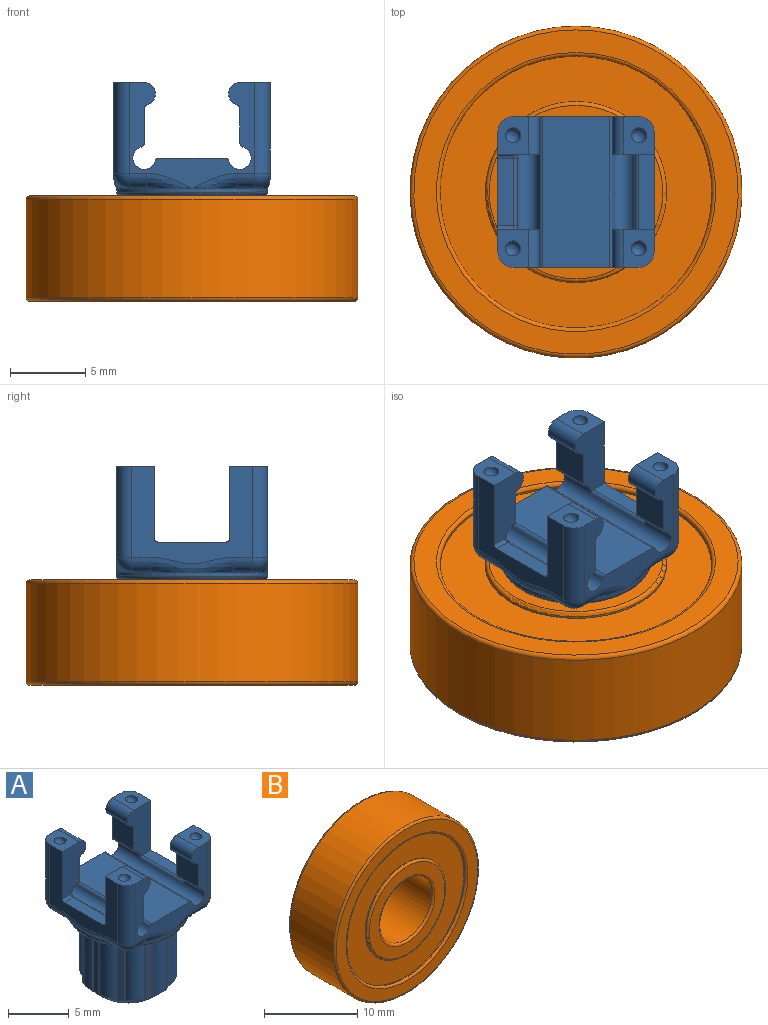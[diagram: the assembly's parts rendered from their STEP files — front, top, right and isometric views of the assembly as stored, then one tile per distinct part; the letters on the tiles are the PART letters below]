
ASSEMBLY  parts=2 mates=1
PART A: 118 faces, bbox 11x11x14.6 mm
  f0: plane 1.25x1.18mm, normal (0,0,-1), area 0.6mm2, adj f39,f105,f110
  f1: plane 1.25x1.18mm, normal (0,0,-1), area 0.6mm2, adj f39,f98,f101
  f2: cylinder r=3.75mm len=6.25mm, axis (0,0,1), area 3.5mm2, adj f40,f52,f88,f90
  f3: cylinder r=3.75mm len=6.25mm, axis (0,0,1), area 3.5mm2, adj f40,f85,f89,f90
  f4: cylinder r=3.75mm len=6.25mm, axis (0,0,1), area 3.5mm2, adj f40,f82,f86,f90
  f5: cylinder r=3.75mm len=6.25mm, axis (0,0,1), area 3.5mm2, adj f40,f79,f83,f90
  f6: cylinder r=3.75mm len=6.25mm, axis (0,0,1), area 3.5mm2, adj f40,f76,f80,f90
  f7: cylinder r=3.75mm len=6.25mm, axis (0,0,1), area 3.5mm2, adj f40,f73,f77,f90
  f8: cylinder r=3.75mm len=6.25mm, axis (0,0,1), area 3.5mm2, adj f40,f70,f74,f90
  f9: cylinder r=3.75mm len=6.25mm, axis (0,0,1), area 3.5mm2, adj f40,f67,f71,f90
  f10: cylinder r=3.75mm len=6.25mm, axis (0,0,1), area 3.5mm2, adj f40,f64,f68,f90
  f11: cylinder r=3.75mm len=6.25mm, axis (0,0,1), area 3.5mm2, adj f40,f51,f65,f90
  f12: plane 1.25x1.18mm, normal (0,0,-1), area 0.6mm2, adj f39,f93,f96
  f13: plane 2.5x2mm, normal (0,0,1), area 4mm2, adj f16,f17,f32,f33,f94,f115
  f14: plane 2.5x2mm, normal (0,0,1), area 4mm2, adj f18,f28,f31,f38,f109,f117
  f15: plane 2.5x2.31mm, normal (1,0,0), area 5.8mm2, adj f32,f33,f42,f44,f54
  f16: cylinder r=0.75mm len=2.5mm, axis (0,1,0), area 5.4mm2, adj f13,f32,f33,f54
  f17: plane 8x6.44mm, normal (-1,0,0), area 24.2mm2, adj f13,f25,f33,f34,f35,f43,f46,f94
  f18: plane 8x6.44mm, normal (1,0,0), area 24.2mm2, adj f14,f27,f36,f37,f38,f104,f109,f110
  f19: cylinder r=0.75mm len=2.5mm, axis (0,1,0), area 5.4mm2, adj f27,f32,f37,f55
  f20: plane 2.5x2.31mm, normal (-1,0,0), area 5.8mm2, adj f32,f37,f55,f56
  f21: cylinder r=0.75mm len=10mm, axis (0,1,0), area 25.7mm2, adj f31,f32,f37,f38,f56,f57,f60,f61
  f22: cylinder r=0.75mm len=10mm, axis (0,1,0), area 25.3mm2, adj f31,f32,f42,f44,f45,f47,f48,f49
  f23: plane 2.5x2.31mm, normal (1,0,0), area 5.8mm2, adj f31,f34,f49,f50,f58
  f24: cylinder r=0.75mm len=2.5mm, axis (0,1,0), area 5.4mm2, adj f25,f31,f34,f58
  f25: plane 2.5x2mm, normal (0,0,1), area 4mm2, adj f17,f24,f31,f34,f99,f116
  f26: plane 1.25x1.18mm, normal (0,0,-1), area 0.6mm2, adj f39,f108,f113
  f27: plane 2.5x2mm, normal (0,0,1), area 4mm2, adj f18,f19,f32,f37,f104,f114
  f28: cylinder r=0.75mm len=2.5mm, axis (0,1,0), area 5.4mm2, adj f14,f31,f38,f59
  f29: plane 2.5x2.31mm, normal (-1,0,0), area 5.8mm2, adj f31,f38,f59,f60
  f30: plane 10x4.41mm, normal (0,0,1), area 44.1mm2, adj f31,f32,f61,f62
  f31: plane 8.49x7.14mm, normal (0,-1,0), area 19.7mm2, adj f14,f21,f22,f23,f24,f25,f28,f29
  f32: plane 8.49x7.14mm, normal (0,1,0), area 19.7mm2, adj f13,f15,f16,f19,f20,f21,f22,f27
  f33: plane 4.75x2.75mm, normal (0,-1,0), area 9.9mm2, adj f13,f15,f16,f17,f43,f44,f54
  f34: plane 4.75x2.75mm, normal (0,1,0), area 9.9mm2, adj f17,f23,f24,f25,f46,f50,f58
  f35: plane 4.5x1.03mm, normal (0,0,1), area 4.6mm2, adj f17,f43,f46,f47
  f36: plane 5x1.03mm, normal (0,0,1), area 5.2mm2, adj f18,f37,f38,f57
  f37: plane 5.19x2.75mm, normal (0,-1,0), area 10.5mm2, adj f18,f19,f20,f21,f27,f36,f55,f56
  f38: plane 5.19x2.75mm, normal (0,1,0), area 10.5mm2, adj f14,f18,f21,f28,f29,f36,f57,f59
  f39: cylinder r=5mm len=10mm, axis (0,0,1), area 7.9mm2, adj f0,f1,f12,f26,f53,f92,f97,f102
  f40: plane 9.5x9.5mm, normal (0,0,-1), area 23.2mm2, adj f2,f3,f4,f5,f6,f7,f8,f9
  f41: cylinder r=1.05mm len=6.21mm, axis (0,0,1), area 10.4mm2, adj f40,f51,f52,f90
  f42: cylinder r=0.25mm len=2.5mm, axis (0,1,0), area 0.8mm2, adj f15,f22,f32,f44
  f43: cylinder r=0.25mm len=1.03mm, axis (-1,0,0), area 0.4mm2, adj f17,f33,f35,f45
  f44: torus R=1mm, axis (0,-1,0), area 0.4mm2, adj f15,f22,f33,f42,f45
  f45: bspline ~0.54x0.49mm, area 0.2mm2, adj f22,f43,f44,f47
  f46: cylinder r=0.25mm len=1.03mm, axis (1,0,0), area 0.4mm2, adj f17,f34,f35,f48
  f47: cylinder r=0.25mm len=4.5mm, axis (0,1,0), area 1.5mm2, adj f22,f35,f45,f48
  f48: bspline ~0.61x0.47mm, area 0.2mm2, adj f22,f46,f47,f50
  f49: cylinder r=0.25mm len=2.5mm, axis (0,1,0), area 0.8mm2, adj f22,f23,f31,f50
  f50: torus R=1mm, axis (0,-1,0), area 0.4mm2, adj f22,f23,f34,f48,f49
  f51: cylinder r=0.25mm len=6.25mm, axis (0,0,-1), area 0.9mm2, adj f11,f40,f41,f90
  f52: cylinder r=0.25mm len=6.25mm, axis (0,0,1), area 0.9mm2, adj f2,f40,f41,f90
  f53: torus R=4.75mm, axis (0,0,1), area 12.1mm2, adj f39,f40
  f54: cylinder r=0.25mm len=2.5mm, axis (0,1,0), area 0.8mm2, adj f15,f16,f32,f33
  f55: cylinder r=0.25mm len=2.5mm, axis (0,1,0), area 0.8mm2, adj f19,f20,f32,f37
  f56: cylinder r=0.25mm len=2.5mm, axis (0,1,0), area 0.8mm2, adj f20,f21,f32,f37
  f57: cylinder r=0.25mm len=5mm, axis (0,1,0), area 1.6mm2, adj f21,f36,f37,f38
  f58: cylinder r=0.25mm len=2.5mm, axis (0,1,0), area 0.8mm2, adj f23,f24,f31,f34
  f59: cylinder r=0.25mm len=2.5mm, axis (0,1,0), area 0.8mm2, adj f28,f29,f31,f38
  f60: cylinder r=0.25mm len=2.5mm, axis (0,1,0), area 0.8mm2, adj f21,f29,f31,f38
  f61: cylinder r=0.25mm len=10mm, axis (0,1,0), area 3.3mm2, adj f21,f30,f31,f32
  f62: cylinder r=0.25mm len=10mm, axis (0,1,0), area 3.3mm2, adj f22,f30,f31,f32
  f63: cylinder r=1.05mm len=6.21mm, axis (0,0,1), area 10.4mm2, adj f40,f64,f65,f90
  f64: cylinder r=0.25mm len=6.25mm, axis (0,0,-1), area 0.9mm2, adj f10,f40,f63,f90
  f65: cylinder r=0.25mm len=6.25mm, axis (0,0,1), area 0.9mm2, adj f11,f40,f63,f90
  f66: cylinder r=1.05mm len=6.21mm, axis (0,0,1), area 10.4mm2, adj f40,f67,f68,f90
  f67: cylinder r=0.25mm len=6.25mm, axis (0,0,-1), area 0.9mm2, adj f9,f40,f66,f90
  f68: cylinder r=0.25mm len=6.25mm, axis (0,0,1), area 0.9mm2, adj f10,f40,f66,f90
  f69: cylinder r=1.05mm len=6.21mm, axis (0,0,1), area 10.4mm2, adj f40,f70,f71,f90
  f70: cylinder r=0.25mm len=6.25mm, axis (0,0,-1), area 0.9mm2, adj f8,f40,f69,f90
  f71: cylinder r=0.25mm len=6.25mm, axis (0,0,1), area 0.9mm2, adj f9,f40,f69,f90
  f72: cylinder r=1.05mm len=6.21mm, axis (0,0,1), area 10.4mm2, adj f40,f73,f74,f90
  f73: cylinder r=0.25mm len=6.25mm, axis (0,0,-1), area 0.9mm2, adj f7,f40,f72,f90
  f74: cylinder r=0.25mm len=6.25mm, axis (0,0,1), area 0.9mm2, adj f8,f40,f72,f90
  f75: cylinder r=1.05mm len=6.21mm, axis (0,0,1), area 10.4mm2, adj f40,f76,f77,f90
  f76: cylinder r=0.25mm len=6.25mm, axis (0,0,-1), area 0.9mm2, adj f6,f40,f75,f90
  f77: cylinder r=0.25mm len=6.25mm, axis (0,0,1), area 0.9mm2, adj f7,f40,f75,f90
  f78: cylinder r=1.05mm len=6.21mm, axis (0,0,1), area 10.4mm2, adj f40,f79,f80,f90
  f79: cylinder r=0.25mm len=6.25mm, axis (0,0,-1), area 0.9mm2, adj f5,f40,f78,f90
  f80: cylinder r=0.25mm len=6.25mm, axis (0,0,1), area 0.9mm2, adj f6,f40,f78,f90
  f81: cylinder r=1.05mm len=6.21mm, axis (0,0,1), area 10.4mm2, adj f40,f82,f83,f90
  f82: cylinder r=0.25mm len=6.25mm, axis (0,0,-1), area 0.9mm2, adj f4,f40,f81,f90
  f83: cylinder r=0.25mm len=6.25mm, axis (0,0,1), area 0.9mm2, adj f5,f40,f81,f90
  f84: cylinder r=1.05mm len=6.21mm, axis (0,0,1), area 10.4mm2, adj f40,f85,f86,f90
  f85: cylinder r=0.25mm len=6.25mm, axis (0,0,-1), area 0.9mm2, adj f3,f40,f84,f90
  f86: cylinder r=0.25mm len=6.25mm, axis (0,0,1), area 0.9mm2, adj f4,f40,f84,f90
  f87: cylinder r=1.05mm len=6.21mm, axis (0,0,1), area 10.4mm2, adj f40,f88,f89,f90
  f88: cylinder r=0.25mm len=6.25mm, axis (0,0,-1), area 0.9mm2, adj f2,f40,f87,f90
  f89: cylinder r=0.25mm len=6.25mm, axis (0,0,1), area 0.9mm2, adj f3,f40,f87,f90
  f90: cone r=3mm half-angle=45deg, axis (0,0,1), area 27.4mm2, adj f2,f3,f4,f5,f6,f7,f8,f9
  f91: plane 6x6mm, normal (0,0,-1), area 28.3mm2, adj f90
  f92: bspline ~3.32x1.16mm, area 2.1mm2, adj f32,f39,f93
  f93: cylinder r=1mm len=1.18mm, axis (1,0,0), area 1.8mm2, adj f12,f32,f92,f95
  f94: cylinder r=1mm len=6mm, axis (0,0,-1), area 9.4mm2, adj f13,f17,f32,f95
  f95: sphere r=1mm, area 1.6mm2, adj f93,f94,f96
  f96: cylinder r=1mm len=1.25mm, axis (0,1,0), area 2mm2, adj f12,f17,f95,f97
  f97: bspline ~5.5x1mm, area 5.3mm2, adj f17,f39,f96,f98
  f98: cylinder r=1mm len=1.25mm, axis (0,1,0), area 2mm2, adj f1,f17,f97,f100
  f99: cylinder r=1mm len=6mm, axis (0,0,1), area 9.4mm2, adj f17,f25,f31,f100
  f100: sphere r=1mm, area 1.6mm2, adj f98,f99,f101
  f101: cylinder r=1mm len=1.18mm, axis (-1,0,0), area 1.8mm2, adj f1,f31,f100,f102
  f102: bspline ~3.32x1.16mm, area 2.1mm2, adj f31,f39,f101
  f103: bspline ~3.32x1.16mm, area 2.1mm2, adj f32,f39,f105
  f104: cylinder r=1mm len=6mm, axis (0,0,1), area 9.4mm2, adj f18,f27,f32,f107
  f105: cylinder r=1mm len=1.18mm, axis (1,0,0), area 1.8mm2, adj f0,f32,f103,f107
  f106: bspline ~3.32x1.16mm, area 2.1mm2, adj f31,f39,f108
  f107: sphere r=1mm, area 1.6mm2, adj f104,f105,f110
  f108: cylinder r=1mm len=1.18mm, axis (-1,0,0), area 1.8mm2, adj f26,f31,f106,f111
  f109: cylinder r=1mm len=6mm, axis (0,0,-1), area 9.4mm2, adj f14,f18,f31,f111
  f110: cylinder r=1mm len=1.25mm, axis (0,-1,0), area 2mm2, adj f0,f18,f107,f112
  f111: sphere r=1mm, area 1.6mm2, adj f108,f109,f113
  f112: bspline ~6.21x1.18mm, area 5.3mm2, adj f18,f39,f110,f113
  f113: cylinder r=1mm len=1.25mm, axis (0,-1,0), area 2mm2, adj f18,f26,f111,f112
  f114: sphere r=0.5mm, area 1.6mm2, adj f27
  f115: sphere r=0.5mm, area 1.6mm2, adj f13
  f116: sphere r=0.5mm, area 1.6mm2, adj f25
  f117: sphere r=0.5mm, area 1.6mm2, adj f14
PART B: 20 faces, bbox 23.8x7x23.8 mm
  f0: cylinder r=9mm len=18mm, axis (0,1,0), area 7.1mm2, adj f1,f19
  f1: plane 18x18mm, normal (0,-1,0), area 141.4mm2, adj f0,f2
  f2: cylinder r=6mm len=12mm, axis (0,1,0), area 4.7mm2, adj f1,f12
  f3: plane 11.5x11.5mm, normal (0,-1,0), area 47.1mm2, adj f12,f13
  f4: cylinder r=4mm len=8mm, axis (0,1,0), area 163.4mm2, adj f13,f14
  f5: plane 11.5x11.5mm, normal (0,1,0), area 47.1mm2, adj f14,f15
  f6: cylinder r=6mm len=12mm, axis (0,1,0), area 4.7mm2, adj f7,f15
  f7: plane 18x18mm, normal (0,1,0), area 141.4mm2, adj f6,f8
  f8: cylinder r=9mm len=18mm, axis (0,1,0), area 7.1mm2, adj f7,f16
  f9: plane 21.5x21.5mm, normal (0,1,0), area 94.2mm2, adj f16,f17
  f10: cylinder r=11mm len=22mm, axis (0,1,0), area 449.2mm2, adj f17,f18
  f11: plane 21.5x21.5mm, normal (0,-1,0), area 94.2mm2, adj f18,f19
  f12: torus R=5.75mm, axis (0,-1,0), area 14.6mm2, adj f2,f3
  f13: torus R=4.25mm, axis (0,-1,0), area 10.1mm2, adj f3,f4
  f14: torus R=4.25mm, axis (0,-1,0), area 10.1mm2, adj f4,f5
  f15: torus R=5.75mm, axis (0,-1,0), area 14.6mm2, adj f5,f6
  f16: torus R=9.25mm, axis (0,1,0), area 22.4mm2, adj f8,f9
  f17: torus R=10.75mm, axis (0,1,0), area 26.9mm2, adj f9,f10
  f18: torus R=10.75mm, axis (0,1,0), area 26.9mm2, adj f10,f11
  f19: torus R=9.25mm, axis (0,1,0), area 22.4mm2, adj f0,f11
PLACE A t=(-14.93,-7.69,8.12)mm
PLACE B rot(axis=(-1,0,0),90deg) t=(-14.93,-7.69,4.12)mm
MATE revolute B.f0 <-> A.f2  axis (0,0,1) through (-14.93,-7.69,7.62)mm
